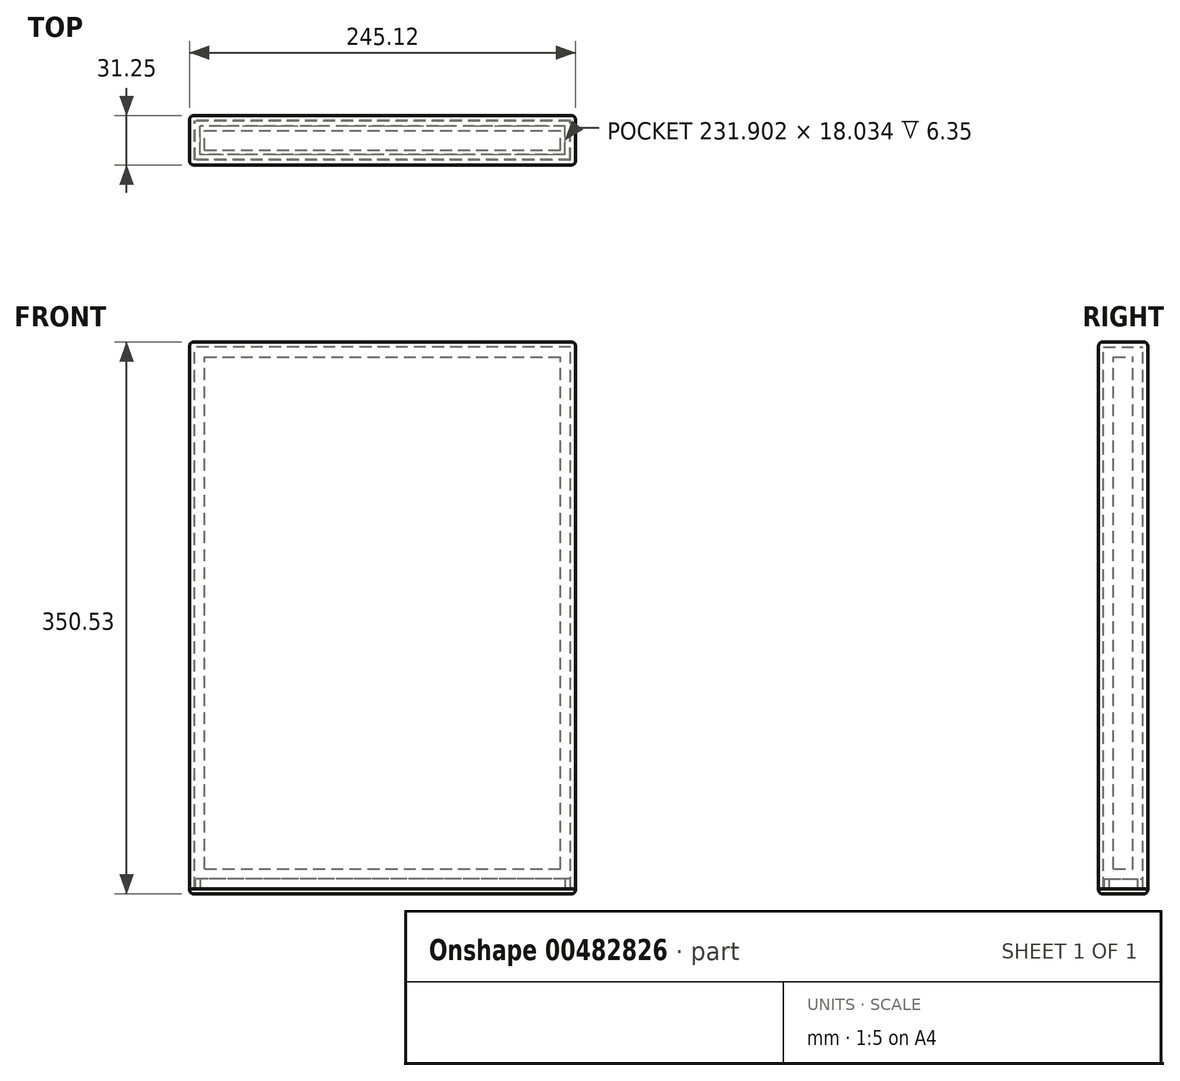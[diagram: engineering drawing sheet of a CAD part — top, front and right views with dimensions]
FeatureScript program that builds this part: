
annotation { "Feature Type Name" : "Feature", "Feature Type Description" : "" }
export const myFeature = defineFeature(function(context is Context, id is Id, definition is map)
    precondition{}
    {
        {
            var Q0;
            Q0=qCreatedBy(makeId("Front.planeOp"),FACE);
            var sketch = newSketch(context, id + "F0", { "sketchPlane" : qUnion([Q0])});
            skLineSegment(sketch, "E0.bottom", {"start": v(0, 0) * mm, "end": v(226.06, 0) * mm});
            skLineSegment(sketch, "E0.top", {"start": v(0, 325.12) * mm, "end": v(226.06, 325.12) * mm});
            skLineSegment(sketch, "E0.left", {"start": v(0, 0) * mm, "end": v(0, 325.12) * mm});
            skLineSegment(sketch, "E0.right", {"start": v(226.06, 0) * mm, "end": v(226.06, 325.12) * mm});
            skSolve(sketch);
        }
        {
            var Q0;
            Q0 = qSketchRegion(id + "F0", true);
            extrude(context, id + "F1", {"entities" : qUnion([Q0]), "depth" : 12.2 * mm});
        }
        {
            var Q0;
            Q0=makeQuery(id+"F1.opExtrude","SWEPT_FACE",FACE,{"disambiguationData":[OSD([sQuery(id+"F0.wireOp",EDGE,"E0.top")])]});
            var sketch = newSketch(context, id + "F2", { "sketchPlane" : qUnion([Q0])});
            skPoint(sketch, "E1.0", {"position": v(0, 0) * mm});
            skPoint(sketch, "E2.0", {"position": v(226.06, -12.2) * mm});
            skLineSegment(sketch, "E3.bottom", {"start": v(232.4, -18.54) * mm, "end": v(-6.35, -18.54) * mm});
            skLineSegment(sketch, "E3.top", {"start": v(232.4, 6.35) * mm, "end": v(-6.35, 6.35) * mm});
            skLineSegment(sketch, "E3.left", {"start": v(232.4, -18.54) * mm, "end": v(232.4, 6.35) * mm});
            skLineSegment(sketch, "E3.right", {"start": v(-6.35, -18.54) * mm, "end": v(-6.35, 6.35) * mm});
            skLineSegment(sketch, "E4.0", {"start": v(235.58, 9.53) * mm, "end": v(-9.53, 9.53) * mm});
            skLineSegment(sketch, "E4.1", {"start": v(235.58, -21.72) * mm, "end": v(235.58, 9.53) * mm});
            skLineSegment(sketch, "E4.2", {"start": v(235.58, -21.72) * mm, "end": v(-9.53, -21.72) * mm});
            skLineSegment(sketch, "E4.3", {"start": v(-9.52, -21.72) * mm, "end": v(-9.53, 9.53) * mm});
            skSolve(sketch);
        }
        {
            var Q0;
            Q0 = qSketchRegion(id + "F2", true);
            extrude(context, id + "F3", {"entities" : qUnion([Q0]), "oppositeDirection" : true, "depth" : 337.82 * mm, "hasSecondDirection" : true, "secondDirectionOppositeDirection" : false, "secondDirectionDepth" : 6.35 * mm});
        }
        {
            var Q0;
            Q0=makeQuery(id+"F3.opExtrude","CAP_FACE",FACE,{"disambiguationData":[OSD([sQuery(id+"F2.wireOp",EDGE,"E3.bottom"),sQuery(id+"F2.wireOp",EDGE,"E3.top"),sQuery(id+"F2.wireOp",EDGE,"E3.left"),sQuery(id+"F2.wireOp",EDGE,"E3.right"),sQuery(id+"F2.wireOp",EDGE,"E4.0"),sQuery(id+"F2.wireOp",EDGE,"E4.1"),sQuery(id+"F2.wireOp",EDGE,"E4.2"),sQuery(id+"F2.wireOp",EDGE,"E4.3")])],"isStart":true});
            var sketch = newSketch(context, id + "F4", { "sketchPlane" : qUnion([Q0])});
            skLineSegment(sketch, "E5.bottom", {"start": v(-9.53, 9.53) * mm, "end": v(235.58, 9.53) * mm});
            skLineSegment(sketch, "E5.top", {"start": v(-9.53, -21.72) * mm, "end": v(235.58, -21.72) * mm});
            skLineSegment(sketch, "E5.left", {"start": v(-9.53, 9.52) * mm, "end": v(-9.53, -21.72) * mm});
            skLineSegment(sketch, "E5.right", {"start": v(235.58, 9.52) * mm, "end": v(235.58, -21.72) * mm});
            skSolve(sketch);
        }
        {
            var Q0;
            Q0 = qSketchRegion(id + "F4", true);
            extrude(context, id + "F5", {"entities" : qUnion([Q0]), "operationType" : NewBodyOperationType.ADD, "depth" : 3.17 * mm});
        }
        {
            var Q0;
            Q0=makeQuery(id+"F3.opExtrude","CAP_FACE",FACE,{"disambiguationData":[OSD([sQuery(id+"F2.wireOp",EDGE,"E3.bottom"),sQuery(id+"F2.wireOp",EDGE,"E3.top"),sQuery(id+"F2.wireOp",EDGE,"E3.left"),sQuery(id+"F2.wireOp",EDGE,"E3.right"),sQuery(id+"F2.wireOp",EDGE,"E4.0"),sQuery(id+"F2.wireOp",EDGE,"E4.1"),sQuery(id+"F2.wireOp",EDGE,"E4.2"),sQuery(id+"F2.wireOp",EDGE,"E4.3")])],"isStart":false});
            var sketch = newSketch(context, id + "F6", { "sketchPlane" : qUnion([Q0])});
            skLineSegment(sketch, "E6.bottom", {"start": v(-9.53, 21.72) * mm, "end": v(235.58, 21.72) * mm});
            skLineSegment(sketch, "E6.top", {"start": v(-9.53, -9.53) * mm, "end": v(235.58, -9.53) * mm});
            skLineSegment(sketch, "E6.left", {"start": v(-9.53, 21.72) * mm, "end": v(-9.53, -9.53) * mm});
            skLineSegment(sketch, "E6.right", {"start": v(235.58, 21.72) * mm, "end": v(235.58, -9.53) * mm});
            skSolve(sketch);
        }
        {
            var Q0;
            Q0 = qSketchRegion(id + "F6", true);
            extrude(context, id + "F7", {"entities" : qUnion([Q0]), "depth" : 3.17 * mm});
        }
        {
            var Q0;
            Q0=makeQuery(id+"F7.opExtrude","CAP_FACE",FACE,{"disambiguationData":[OSD([sQuery(id+"F6.wireOp",EDGE,"E6.bottom"),sQuery(id+"F6.wireOp",EDGE,"E6.top"),sQuery(id+"F6.wireOp",EDGE,"E6.left"),sQuery(id+"F6.wireOp",EDGE,"E6.right")])],"isStart":true});
            var sketch = newSketch(context, id + "F8", { "sketchPlane" : qUnion([Q0])});
            skLineSegment(sketch, "E7.0", {"start": v(232.4, 6.35) * mm, "end": v(-6.35, 6.35) * mm, "construction": true});
            skLineSegment(sketch, "E8.0", {"start": v(232.4, -18.54) * mm, "end": v(-6.35, -18.54) * mm, "construction": true});
            skLineSegment(sketch, "E9.0", {"start": v(232.4, -18.54) * mm, "end": v(232.4, 6.35) * mm, "construction": true});
            skLineSegment(sketch, "E10.0", {"start": v(-6.35, -18.54) * mm, "end": v(-6.35, 6.35) * mm, "construction": true});
            skLineSegment(sketch, "E11.0", {"start": v(232.16, -18.29) * mm, "end": v(-6.1, -18.29) * mm});
            skLineSegment(sketch, "E11.1", {"start": v(232.16, -18.29) * mm, "end": v(232.16, 6.1) * mm});
            skLineSegment(sketch, "E11.2", {"start": v(232.16, 6.1) * mm, "end": v(-6.1, 6.1) * mm});
            skLineSegment(sketch, "E11.3", {"start": v(-6.1, -18.29) * mm, "end": v(-6.1, 6.1) * mm});
            skLineSegment(sketch, "E12.0", {"start": v(228.98, 2.92) * mm, "end": v(-2.92, 2.92) * mm});
            skLineSegment(sketch, "E12.1", {"start": v(228.98, -15.11) * mm, "end": v(228.98, 2.92) * mm});
            skLineSegment(sketch, "E12.2", {"start": v(228.98, -15.11) * mm, "end": v(-2.92, -15.11) * mm});
            skLineSegment(sketch, "E12.3", {"start": v(-2.92, -15.11) * mm, "end": v(-2.92, 2.92) * mm});
            skSolve(sketch);
        }
        {
            var Q0;
            Q0=makeQuery(id+"F8.imprint","IMPRINT",FACE,{"disambiguationData":[TD([[makeQuery(id+"F8.imprint","IMPRINT",EDGE,{"derivedFrom":sQuery(id+"F8.wireOp",EDGE,"E11.0")}),-1.0]])]});
            extrude(context, id + "F9", {"entities" : qUnion([Q0]), "operationType" : NewBodyOperationType.ADD, "depth" : 6.35 * mm});
        }
        {
            var Q0;
            Q0=makeQuery(id+"F7.opExtrude","CAP_EDGE",EDGE,{"disambiguationData":[OSD([sQuery(id+"F6.wireOp",EDGE,"E6.right")])],"isStart":false});
            fillet(context, id + "F10", {"entities" : qUnion([Q0]), "radius" : 2.54 * mm, "tangentPropagation" : true, "allowEdgeOverflow" : false});
        }
        {
            var Q0;
            Q0=makeQuery(id+"F5.boolean.opBoolean","MERGE",EDGE,{"derivedFrom":[makeQuery(id+"F3.opExtrude","SWEPT_EDGE",EDGE,{"disambiguationData":[OSD([sQuery(id+"F2.wireOp",EDGE,"E4.1"),sQuery(id+"F2.wireOp",EDGE,"E4.2")])]}),makeQuery(id+"F5.opExtrude","SWEPT_EDGE",EDGE,{"disambiguationData":[OSD([sQuery(id+"F4.wireOp",EDGE,"E5.top"),sQuery(id+"F4.wireOp",EDGE,"E5.right")])]})]});
            var Q1;
            Q1=makeQuery(id+"F7.opExtrude","CAP_EDGE",EDGE,{"disambiguationData":[OSD([sQuery(id+"F6.wireOp",EDGE,"E6.top")])],"isStart":false});
            fillet(context, id + "F11", {"entities" : qUnion([Q0, Q1]), "radius" : 2.54 * mm, "tangentPropagation" : true, "allowEdgeOverflow" : false});
        }
        {
            var Q0;
            Q0=makeQuery(id+"F11.opFillet","BLEND_EDGE",EDGE,{"blendedFrom":[makeQuery(id+"F7.opExtrude","CAP_EDGE",EDGE,{"disambiguationData":[OSD([sQuery(id+"F6.wireOp",EDGE,"E6.top")])],"isStart":false}),makeQuery(id+"F10.opFillet","BLEND_FACE",FACE,{"disambiguationData":[OSD([sQuery(id+"F6.wireOp",EDGE,"E6.right")])]})],"blendedInto":[makeQuery(id+"F10.opFillet","BLEND_FACE",FACE,{"disambiguationData":[OSD([sQuery(id+"F6.wireOp",EDGE,"E6.right")])]})]});
            var Q1;
            Q1=makeQuery(id+"F5.boolean.opBoolean","MERGE",EDGE,{"derivedFrom":[makeQuery(id+"F3.opExtrude","SWEPT_EDGE",EDGE,{"disambiguationData":[OSD([sQuery(id+"F2.wireOp",EDGE,"E4.0"),sQuery(id+"F2.wireOp",EDGE,"E4.1")])]}),makeQuery(id+"F5.opExtrude","SWEPT_EDGE",EDGE,{"disambiguationData":[OSD([sQuery(id+"F4.wireOp",EDGE,"E5.bottom"),sQuery(id+"F4.wireOp",EDGE,"E5.right")])]})]});
            fillet(context, id + "F12", {"entities" : qUnion([Q0, Q1]), "radius" : 2.54 * mm, "tangentPropagation" : true, "allowEdgeOverflow" : false});
        }
        {
            var Q0;
            Q0=makeQuery(id+"F7.opExtrude","CAP_EDGE",EDGE,{"disambiguationData":[OSD([sQuery(id+"F6.wireOp",EDGE,"E6.bottom")])],"isStart":false});
            var Q1;
            Q1=makeQuery(id+"F10.opFillet","BLEND_EDGE",EDGE,{"blendedFrom":[makeQuery(id+"F7.opExtrude","CAP_EDGE",EDGE,{"disambiguationData":[OSD([sQuery(id+"F6.wireOp",EDGE,"E6.right")])],"isStart":false}),makeQuery(id+"F7.opExtrude","SWEPT_FACE",FACE,{"disambiguationData":[OSD([sQuery(id+"F6.wireOp",EDGE,"E6.bottom")])]})],"blendedInto":[makeQuery(id+"F7.opExtrude","SWEPT_FACE",FACE,{"disambiguationData":[OSD([sQuery(id+"F6.wireOp",EDGE,"E6.bottom")])]})]});
            fillet(context, id + "F13", {"entities" : qUnion([Q0, Q1]), "radius" : 2.54 * mm, "tangentPropagation" : true, "allowEdgeOverflow" : false});
        }
        {
            var Q0;
            Q0=makeQuery(id+"F7.opExtrude","CAP_EDGE",EDGE,{"disambiguationData":[OSD([sQuery(id+"F6.wireOp",EDGE,"E6.left")])],"isStart":false});
            fillet(context, id + "F14", {"entities" : qUnion([Q0]), "radius" : 2.54 * mm, "tangentPropagation" : true, "allowEdgeOverflow" : false});
        }
        {
            var Q0;
            Q0=makeQuery(id+"F5.boolean.opBoolean","MERGE",EDGE,{"derivedFrom":[makeQuery(id+"F3.opExtrude","SWEPT_EDGE",EDGE,{"disambiguationData":[OSD([sQuery(id+"F2.wireOp",EDGE,"E4.2"),sQuery(id+"F2.wireOp",EDGE,"E4.3")])]}),makeQuery(id+"F5.opExtrude","SWEPT_EDGE",EDGE,{"disambiguationData":[OSD([sQuery(id+"F4.wireOp",EDGE,"E5.top"),sQuery(id+"F4.wireOp",EDGE,"E5.left")])]})]});
            fillet(context, id + "F15", {"entities" : qUnion([Q0]), "radius" : 2.54 * mm, "tangentPropagation" : true, "allowEdgeOverflow" : false});
        }
        {
            var Q0;
            {var subQ0=sQuery(id+"F4.wireOp",EDGE,"E5.right");var subQ1=sQuery(id+"F4.wireOp",EDGE,"E5.top");Q0=makeQuery(id+"F11.opFillet","BLEND_EDGE",EDGE,{"blendedFrom":[makeQuery(id+"F5.boolean.opBoolean","MERGE",EDGE,{"derivedFrom":[makeQuery(id+"F3.opExtrude","SWEPT_EDGE",EDGE,{"disambiguationData":[OSD([sQuery(id+"F2.wireOp",EDGE,"E4.1"),sQuery(id+"F2.wireOp",EDGE,"E4.2")])]}),makeQuery(id+"F5.opExtrude","SWEPT_EDGE",EDGE,{"disambiguationData":[OSD([subQ1,subQ0])]})]}),makeQuery(id+"F5.opExtrude","CAP_FACE",FACE,{"disambiguationData":[OSD([sQuery(id+"F4.wireOp",EDGE,"E5.bottom"),subQ1,sQuery(id+"F4.wireOp",EDGE,"E5.left"),subQ0])],"isStart":false})],"blendedInto":[makeQuery(id+"F5.opExtrude","CAP_FACE",FACE,{"disambiguationData":[OSD([sQuery(id+"F4.wireOp",EDGE,"E5.bottom"),subQ1,sQuery(id+"F4.wireOp",EDGE,"E5.left"),subQ0])],"isStart":false})]});}
            var Q1;
            Q1=makeQuery(id+"F5.opExtrude","CAP_EDGE",EDGE,{"disambiguationData":[OSD([sQuery(id+"F4.wireOp",EDGE,"E5.top")])],"isStart":false});
            var Q2;
            Q2=makeQuery(id+"F5.opExtrude","CAP_EDGE",EDGE,{"disambiguationData":[OSD([sQuery(id+"F4.wireOp",EDGE,"E5.right")])],"isStart":false});
            var Q3;
            {var subQ0=sQuery(id+"F4.wireOp",EDGE,"E5.right");var subQ1=sQuery(id+"F4.wireOp",EDGE,"E5.bottom");Q3=makeQuery(id+"F12.opFillet","BLEND_EDGE",EDGE,{"blendedFrom":[makeQuery(id+"F5.boolean.opBoolean","MERGE",EDGE,{"derivedFrom":[makeQuery(id+"F3.opExtrude","SWEPT_EDGE",EDGE,{"disambiguationData":[OSD([sQuery(id+"F2.wireOp",EDGE,"E4.0"),sQuery(id+"F2.wireOp",EDGE,"E4.1")])]}),makeQuery(id+"F5.opExtrude","SWEPT_EDGE",EDGE,{"disambiguationData":[OSD([subQ1,subQ0])]})]}),makeQuery(id+"F5.opExtrude","CAP_FACE",FACE,{"disambiguationData":[OSD([subQ1,sQuery(id+"F4.wireOp",EDGE,"E5.top"),sQuery(id+"F4.wireOp",EDGE,"E5.left"),subQ0])],"isStart":false})],"blendedInto":[makeQuery(id+"F5.opExtrude","CAP_FACE",FACE,{"disambiguationData":[OSD([subQ1,sQuery(id+"F4.wireOp",EDGE,"E5.top"),sQuery(id+"F4.wireOp",EDGE,"E5.left"),subQ0])],"isStart":false})]});}
            var Q4;
            Q4=makeQuery(id+"F5.opExtrude","CAP_EDGE",EDGE,{"disambiguationData":[OSD([sQuery(id+"F4.wireOp",EDGE,"E5.bottom")])],"isStart":false});
            fillet(context, id + "F16", {"entities" : qUnion([Q0, Q1, Q2, Q3, Q4]), "radius" : 2.54 * mm, "tangentPropagation" : true, "allowEdgeOverflow" : false});
        }
        {
            var Q0;
            Q0=makeQuery(id+"F16.opFillet","BLEND_EDGE",EDGE,{"blendedFrom":[makeQuery(id+"F5.opExtrude","CAP_EDGE",EDGE,{"disambiguationData":[OSD([sQuery(id+"F4.wireOp",EDGE,"E5.bottom")])],"isStart":false}),makeQuery(id+"F5.opExtrude","CAP_EDGE",EDGE,{"disambiguationData":[OSD([sQuery(id+"F4.wireOp",EDGE,"E5.left")])],"isStart":false})],"blendedInto":[]});
            fillet(context, id + "F17", {"entities" : qUnion([Q0]), "radius" : 2.54 * mm, "tangentPropagation" : true, "allowEdgeOverflow" : false});
        }
    });
